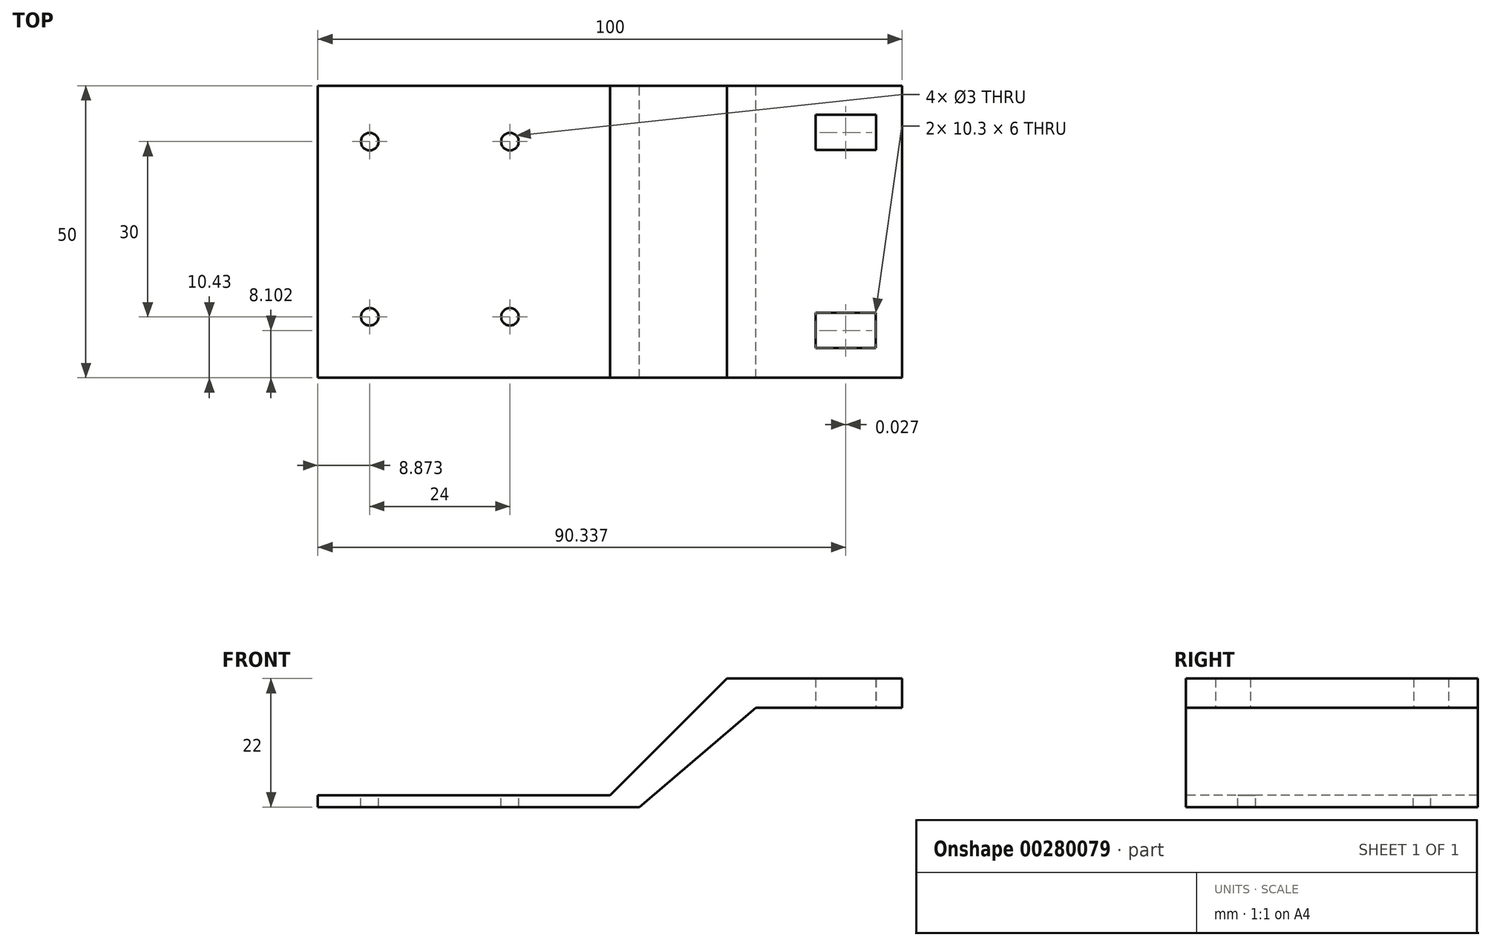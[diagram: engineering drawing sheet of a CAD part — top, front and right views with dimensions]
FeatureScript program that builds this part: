
annotation { "Feature Type Name" : "Feature", "Feature Type Description" : "" }
export const myFeature = defineFeature(function(context is Context, id is Id, definition is map)
    precondition{}
    {
        {
            var Q0;
            Q0=qCreatedBy(makeId("Top.planeOp"),FACE);
            var sketch = newSketch(context, id + "F0", { "sketchPlane" : qUnion([Q0])});
            skLineSegment(sketch, "E0.bottom", {"start": v(0, 0) * mm, "end": v(50, 0) * mm});
            skLineSegment(sketch, "E0.top", {"start": v(0, -50) * mm, "end": v(50, -50) * mm});
            skLineSegment(sketch, "E0.left", {"start": v(0, 0) * mm, "end": v(0, -50) * mm});
            skLineSegment(sketch, "E0.right", {"start": v(50, 0) * mm, "end": v(50, -50) * mm});
            skSolve(sketch);
        }
        {
            var Q0;
            Q0=makeQuery(id+"F0.imprint","IMPRINT",FACE,{"disambiguationData":[TD([[makeQuery(id+"F0.imprint","IMPRINT",EDGE,{"derivedFrom":sQuery(id+"F0.wireOp",EDGE,"E0.bottom")}),-1.0]])]});
            extrude(context, id + "F1", {"entities" : qUnion([Q0]), "depth" : 2 * mm});
        }
        {
            var Q0;
            Q0=makeQuery(id+"F1.opExtrude","CAP_FACE",FACE,{"disambiguationData":[OSD([sQuery(id+"F0.wireOp",EDGE,"E0.bottom"),sQuery(id+"F0.wireOp",EDGE,"E0.top"),sQuery(id+"F0.wireOp",EDGE,"E0.left"),sQuery(id+"F0.wireOp",EDGE,"E0.right")])],"isStart":false});
            var sketch = newSketch(context, id + "F2", { "sketchPlane" : qUnion([Q0])});
            skLineSegment(sketch, "E1.bottom", {"start": v(50, 0) * mm, "end": v(25, 0) * mm});
            skLineSegment(sketch, "E1.top", {"start": v(50, -50) * mm, "end": v(25, -50) * mm});
            skLineSegment(sketch, "E1.left", {"start": v(50, 0) * mm, "end": v(50, -50) * mm});
            skLineSegment(sketch, "E1.right", {"start": v(25, 0) * mm, "end": v(25, -50) * mm});
            skSolve(sketch);
        }
        {
            var Q0;
            Q0 = qSketchRegion(id + "F2", true);
            extrude(context, id + "F3", {"entities" : qUnion([Q0]), "operationType" : NewBodyOperationType.ADD, "depth" : 20 * mm});
        }
        {
            var Q0;
            Q0=makeQuery(id+"F3.boolean.opBoolean","MERGE",FACE,{"derivedFrom":[makeQuery(id+"F1.opExtrude","SWEPT_FACE",FACE,{"disambiguationData":[OSD([sQuery(id+"F0.wireOp",EDGE,"E0.right")])]}),makeQuery(id+"F3.opExtrude","SWEPT_FACE",FACE,{"disambiguationData":[OSD([sQuery(id+"F2.wireOp",EDGE,"E1.left")])]})]});
            var sketch = newSketch(context, id + "F4", { "sketchPlane" : qUnion([Q0])});
            skLineSegment(sketch, "E2.bottom", {"start": v(-50, 22) * mm, "end": v(0, 22) * mm});
            skLineSegment(sketch, "E2.top", {"start": v(-50, 17) * mm, "end": v(0, 17) * mm});
            skLineSegment(sketch, "E2.left", {"start": v(-50, 22) * mm, "end": v(-50, 17) * mm});
            skLineSegment(sketch, "E2.right", {"start": v(0, 22) * mm, "end": v(0, 17) * mm});
            skSolve(sketch);
        }
        {
            var Q0;
            Q0 = qSketchRegion(id + "F4", true);
            extrude(context, id + "F5", {"entities" : qUnion([Q0]), "operationType" : NewBodyOperationType.ADD, "depth" : 25 * mm});
        }
        {
            var Q0;
            Q0=makeQuery(id+"F5.boolean.opBoolean","MERGE",FACE,{"derivedFrom":[makeQuery(id+"F3.boolean.opBoolean","MERGE",FACE,{"derivedFrom":[makeQuery(id+"F1.opExtrude","SWEPT_FACE",FACE,{"disambiguationData":[OSD([sQuery(id+"F0.wireOp",EDGE,"E0.top")])]}),makeQuery(id+"F3.opExtrude","SWEPT_FACE",FACE,{"disambiguationData":[OSD([sQuery(id+"F2.wireOp",EDGE,"E1.top")])]})]}),makeQuery(id+"F5.opExtrude","SWEPT_FACE",FACE,{"disambiguationData":[OSD([sQuery(id+"F4.wireOp",EDGE,"E2.left")])]})]});
            var sketch = newSketch(context, id + "F6", { "sketchPlane" : qUnion([Q0])});
            skLineSegment(sketch, "E3", {"start": v(25, 22) * mm, "end": v(25, 2) * mm});
            skLineSegment(sketch, "E4", {"start": v(25, 2) * mm, "end": v(45, 22) * mm});
            skLineSegment(sketch, "E5", {"start": v(45, 22) * mm, "end": v(25, 22) * mm});
            skSolve(sketch);
        }
        {
            var Q0;
            Q0 = qSketchRegion(id + "F6", true);
            extrude(context, id + "F7", {"entities" : qUnion([Q0]), "operationType" : NewBodyOperationType.REMOVE, "oppositeDirection" : true, "depth" : 50 * mm});
        }
        {
            var Q0;
            Q0=makeQuery(id+"F5.opExtrude","SWEPT_FACE",FACE,{"disambiguationData":[OSD([sQuery(id+"F4.wireOp",EDGE,"E2.top")])]});
            var sketch = newSketch(context, id + "F8", { "sketchPlane" : qUnion([Q0])});
            skLineSegment(sketch, "E6.bottom", {"start": v(60.21, 11) * mm, "end": v(70.51, 11) * mm});
            skLineSegment(sketch, "E6.top", {"start": v(60.21, 5) * mm, "end": v(70.51, 5) * mm});
            skLineSegment(sketch, "E6.left", {"start": v(60.21, 11) * mm, "end": v(60.21, 5) * mm});
            skLineSegment(sketch, "E6.right", {"start": v(70.51, 11) * mm, "end": v(70.51, 5) * mm});
            skLineSegment(sketch, "E7.bottom", {"start": v(62.5, 0) * mm, "end": v(65.83, 0) * mm});
            skLineSegment(sketch, "E7.top", {"start": v(62.5, 5) * mm, "end": v(65.83, 5) * mm});
            skLineSegment(sketch, "E7.left", {"start": v(62.5, 0) * mm, "end": v(62.5, 5) * mm});
            skLineSegment(sketch, "E7.right", {"start": v(65.83, 0) * mm, "end": v(65.83, 5) * mm});
            skLineSegment(sketch, "E8.bottom", {"start": v(60.19, 44.9) * mm, "end": v(70.49, 44.9) * mm});
            skLineSegment(sketch, "E8.top", {"start": v(60.19, 38.9) * mm, "end": v(70.49, 38.9) * mm});
            skLineSegment(sketch, "E8.left", {"start": v(60.19, 44.9) * mm, "end": v(60.19, 38.9) * mm});
            skLineSegment(sketch, "E8.right", {"start": v(70.49, 44.9) * mm, "end": v(70.49, 38.9) * mm});
            skSolve(sketch);
        }
        {
            var Q0;
            Q0 = qSketchRegion(id + "F8", true);
            extrude(context, id + "F9", {"entities" : qUnion([Q0]), "operationType" : NewBodyOperationType.REMOVE, "oppositeDirection" : true, "depth" : 50 * mm});
        }
        {
            var Q0;
            Q0=makeQuery(id+"F5.opExtrude","SWEPT_FACE",FACE,{"disambiguationData":[OSD([sQuery(id+"F4.wireOp",EDGE,"E2.top")])]});
            var sketch = newSketch(context, id + "F10", { "sketchPlane" : qUnion([Q0])});
            skLineSegment(sketch, "E9.bottom", {"start": v(62.5, 5) * mm, "end": v(65.83, 5) * mm});
            skLineSegment(sketch, "E9.top", {"start": v(62.5, 0) * mm, "end": v(65.83, 0) * mm});
            skLineSegment(sketch, "E9.left", {"start": v(62.5, 5) * mm, "end": v(62.5, 0) * mm});
            skLineSegment(sketch, "E9.right", {"start": v(65.83, 5) * mm, "end": v(65.83, 0) * mm});
            skSolve(sketch);
        }
        {
            var Q0;
            Q0 = qSketchRegion(id + "F10", true);
            extrude(context, id + "F11", {"entities" : qUnion([Q0]), "operationType" : NewBodyOperationType.ADD, "oppositeDirection" : true, "depth" : 5 * mm});
        }
        {
            var Q0;
            {var subQ3=sQuery(id+"F2.wireOp",EDGE,"E1.bottom");var subQ5=sQuery(id+"F4.wireOp",EDGE,"E2.right");var subQ8=sQuery(id+"F0.wireOp",EDGE,"E0.bottom");var subQ9=makeQuery(id+"F5.boolean.opBoolean","MERGE",FACE,{"derivedFrom":[makeQuery(id+"F3.boolean.opBoolean","MERGE",FACE,{"derivedFrom":[makeQuery(id+"F1.opExtrude","SWEPT_FACE",FACE,{"disambiguationData":[OSD([subQ8])]}),makeQuery(id+"F3.opExtrude","SWEPT_FACE",FACE,{"disambiguationData":[OSD([subQ3])]})]}),makeQuery(id+"F5.opExtrude","SWEPT_FACE",FACE,{"disambiguationData":[OSD([subQ5])]})]});var subQ11=sQuery(id+"F0.wireOp",EDGE,"E0.left");Q0=makeQuery(id+"F11.boolean.opBoolean","MERGE",FACE,{"derivedFrom":[makeQuery(id+"F9.boolean.opBoolean","SPLIT",FACE,{"disambiguationData":[TD([makeQuery(id+"F1.opExtrude","SWEPT_FACE",FACE,{"disambiguationData":[OSD([subQ11])]})])],"derivedFrom":subQ9}),makeQuery(id+"F9.boolean.opBoolean","SPLIT",FACE,{"disambiguationData":[TD([makeQuery(id+"F9.opExtrude","SWEPT_FACE",FACE,{"disambiguationData":[OSD([sQuery(id+"F8.wireOp",EDGE,"E7.right")])]})])],"derivedFrom":subQ9}),makeQuery(id+"F11.opExtrude","SWEPT_FACE",FACE,{"disambiguationData":[OSD([sQuery(id+"F10.wireOp",EDGE,"E9.top")])]})]});}
            var sketch = newSketch(context, id + "F12", { "sketchPlane" : qUnion([Q0])});
            skLineSegment(sketch, "E10", {"start": v(-50, 17) * mm, "end": v(-50, 0) * mm});
            skLineSegment(sketch, "E11", {"start": v(-50, 0) * mm, "end": v(-30, 0) * mm});
            skLineSegment(sketch, "E12", {"start": v(-30, 0) * mm, "end": v(-50, 17) * mm});
            skSolve(sketch);
        }
        {
            var Q0;
            Q0 = qSketchRegion(id + "F12", true);
            extrude(context, id + "F13", {"entities" : qUnion([Q0]), "operationType" : NewBodyOperationType.REMOVE, "oppositeDirection" : true, "depth" : 50 * mm});
        }
        {
            var Q0;
            Q0=makeQuery(id+"F1.opExtrude","SWEPT_FACE",FACE,{"disambiguationData":[OSD([sQuery(id+"F0.wireOp",EDGE,"E0.left")])]});
            var sketch = newSketch(context, id + "F14", { "sketchPlane" : qUnion([Q0])});
            skLineSegment(sketch, "E13.bottom", {"start": v(0, 0) * mm, "end": v(50, 0) * mm});
            skLineSegment(sketch, "E13.top", {"start": v(0, 2) * mm, "end": v(50, 2) * mm});
            skLineSegment(sketch, "E13.left", {"start": v(0, 0) * mm, "end": v(0, 2) * mm});
            skLineSegment(sketch, "E13.right", {"start": v(50, 0) * mm, "end": v(50, 2) * mm});
            skSolve(sketch);
        }
        {
            var Q0;
            Q0 = qSketchRegion(id + "F14", true);
            extrude(context, id + "F15", {"entities" : qUnion([Q0]), "operationType" : NewBodyOperationType.ADD, "depth" : 25 * mm});
        }
        {
            var Q0;
            Q0=makeQuery(id+"F15.boolean.opBoolean","MERGE",FACE,{"derivedFrom":[makeQuery(id+"F1.opExtrude","CAP_FACE",FACE,{"disambiguationData":[OSD([sQuery(id+"F0.wireOp",EDGE,"E0.bottom"),sQuery(id+"F0.wireOp",EDGE,"E0.top"),sQuery(id+"F0.wireOp",EDGE,"E0.left"),sQuery(id+"F0.wireOp",EDGE,"E0.right")])],"isStart":false}),makeQuery(id+"F15.opExtrude","SWEPT_FACE",FACE,{"disambiguationData":[OSD([sQuery(id+"F14.wireOp",EDGE,"E13.top")])]})]});
            var sketch = newSketch(context, id + "F16", { "sketchPlane" : qUnion([Q0])});
            skCircle(sketch, "E14", {"center": v(-16.13, -9.57) * mm, "radius": 1.5 * mm});
            skCircle(sketch, "E15", {"center": v(7.87, -9.57) * mm, "radius": 1.5 * mm});
            skCircle(sketch, "E16", {"center": v(7.87, -39.57) * mm, "radius": 1.5 * mm});
            skCircle(sketch, "E17", {"center": v(-16.13, -39.57) * mm, "radius": 1.5 * mm});
            skSolve(sketch);
        }
        {
            var Q0;
            Q0 = qSketchRegion(id + "F16", true);
            extrude(context, id + "F17", {"entities" : qUnion([Q0]), "operationType" : NewBodyOperationType.REMOVE, "oppositeDirection" : true, "depth" : 50 * mm});
        }
    });
